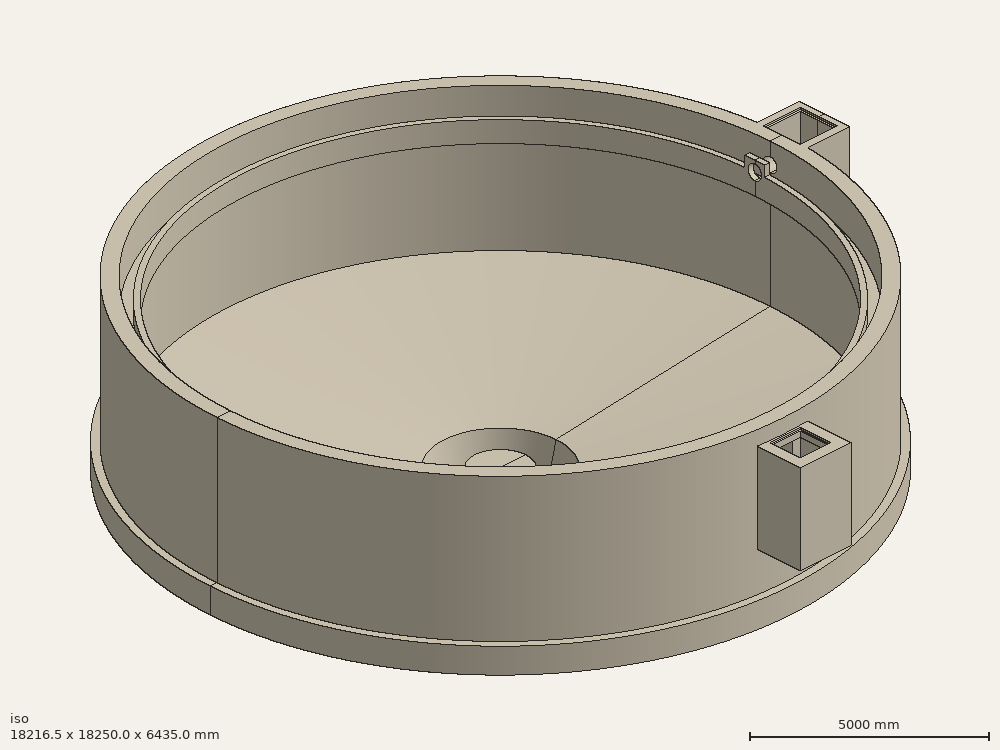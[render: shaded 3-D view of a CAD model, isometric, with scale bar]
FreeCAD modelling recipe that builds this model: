
FCSTD DOCUMENT  (FreeCAD 1.0R39109 (Git))
Label: body16.0m
License: All rights reserved
LicenseURL: https://en.wikipedia.org/wiki/All_rights_reserved
objects: Part::Feature×3, Part::FeaturePython×3, Part::MultiFuse×1, Part::Part2DObjectPython×1, App::DocumentObjectGroup×1, App::Part×1
note: 8 computed .brp shape members not serialized (recipe doc carries the construction recipe); baked Part::Feature solids carry a one-line shape summary decoded from their .brp

FEATURE [Part::Feature] Part__Feature  label="\X2\7D426C888EAF4F5353F3\X0\_1600 v6"
  shape: bbox 18220 x 18250 x 6435 mm, 67 faces (baked)
FEATURE [Part::Feature] Part__Feature001  label="\X2\7D426C888EAF4F5353F3\X0\_1600 v007"
  shape: bbox 1000 x 1000 x 165 mm, 5 faces (baked)
FEATURE [Part::Feature] Part__Feature002  label="\X2\7D426C888EAF4F5353F3\X0\_1600 v008"
  shape: bbox 1000 x 1000 x 165 mm, 5 faces (baked)
FEATURE [Part::MultiFuse] Fusion
  Refine = true
  Shapes = -> [Part__Feature,Part__Feature001,Part__Feature002]
FEATURE [Part::Part2DObjectPython] Rectangle  # Draft 2D object (typed FeaturePython)
  Area = 1.664e+08
  ChamferSize = 0
  Columns = 1
  FilletRadius = 0
  Height = 8504.3
  Length = 19566.5
  MakeFace = true
  Placement = pos=(-9590.65,4.104e-13,-1635.98) rot=(1,0,0;1.5708rad)
  Rows = 1
FEATURE [Part::FeaturePython] Slice  # WARN: FeaturePython — macro-defined, semantics opaque (R4)
  Base = -> Fusion
  Mode = 1
  Tolerance = 0
  Tools = -> [Rectangle]
FEATURE [Part::FeaturePython] Slice_child0  label="Slice.0"  # WARN: FeaturePython — macro-defined, semantics opaque (R4)
  Base = -> Slice
  FilterType = 1
  Invert = false
  OverrideMaxVal = 0
  WindowFrom = 80
  WindowTo = 100
  items = 0
FEATURE [Part::FeaturePython] Slice_child1  label="Slice.1"  # WARN: FeaturePython — macro-defined, semantics opaque (R4)
  Base = -> Slice
  FilterType = 1
  Invert = false
  OverrideMaxVal = 0
  WindowFrom = 80
  WindowTo = 100
  items = 1
FEATURE [App::DocumentObjectGroup] GrExplode_Slice  label="Exploded Slice"
  Group = -> [Slice_child0,Slice_child1]
FEATURE [App::Part] _X2_7D426C888EAF4F5353F3_X0__1600_v6  label="body16.0m"
  Group = -> [Part__Feature,Part__Feature002,Part__Feature001,Fusion,Rectangle,Slice_child0,Slice,Slice_child1,GrExplode_Slice]
  Origin = -> Origin
